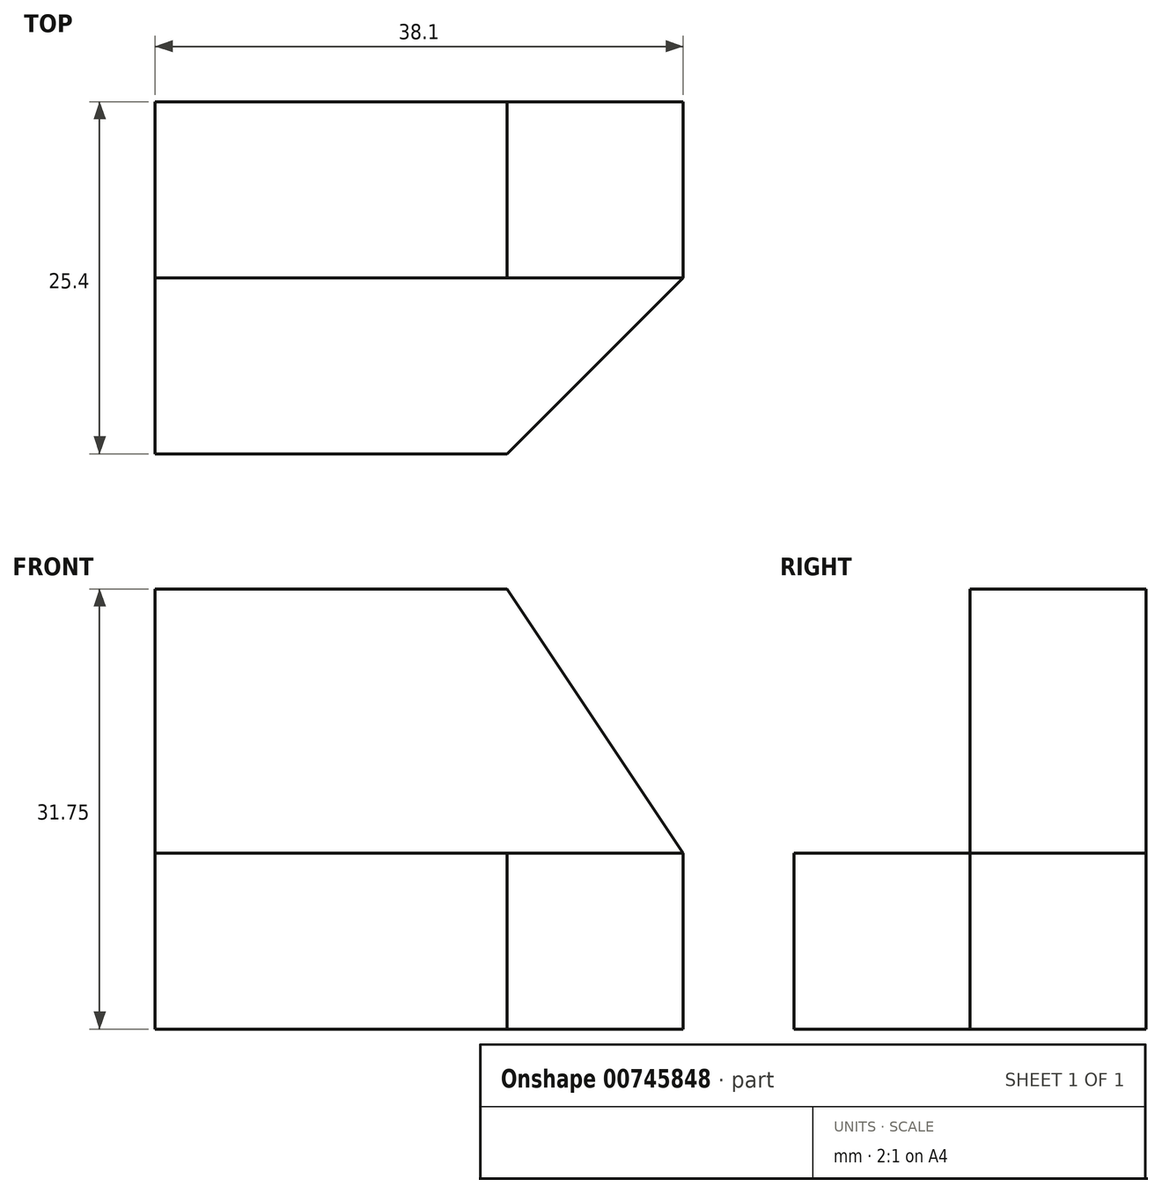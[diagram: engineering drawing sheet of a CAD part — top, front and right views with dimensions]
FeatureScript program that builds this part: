
annotation { "Feature Type Name" : "Feature", "Feature Type Description" : "" }
export const myFeature = defineFeature(function(context is Context, id is Id, definition is map)
    precondition{}
    {
        {
            var Q0;
            Q0=qCreatedBy(makeId("Front.planeOp"),FACE);
            var sketch = newSketch(context, id + "F0", { "sketchPlane" : qUnion([Q0])});
            skLineSegment(sketch, "E0", {"start": v(0, 0) * mm, "end": v(0, 31.75) * mm});
            skLineSegment(sketch, "E1", {"start": v(0, 31.75) * mm, "end": v(38.1, 31.75) * mm});
            skLineSegment(sketch, "E2", {"start": v(38.1, 31.75) * mm, "end": v(38.1, 0) * mm});
            skLineSegment(sketch, "E3", {"start": v(38.1, 0) * mm, "end": v(0, 0) * mm});
            skSolve(sketch);
        }
        {
            var Q0;
            Q0 = qSketchRegion(id + "F0", true);
            extrude(context, id + "F1", {"entities" : qUnion([Q0]), "depth" : 25.4 * mm, "offsetDistance" : 25.4 * mm});
        }
        {
            var Q0;
            Q0=makeQuery(id+"F1.opExtrude","SWEPT_FACE",FACE,{"disambiguationData":[OSD([sQuery(id+"F0.wireOp",EDGE,"E1")])]});
            var sketch = newSketch(context, id + "F2", { "sketchPlane" : qUnion([Q0])});
            skLineSegment(sketch, "E4", {"start": v(0, -12.7) * mm, "end": v(38.1, -12.7) * mm});
            skSolve(sketch);
        }
        {
            var Q0;
            {var subQ0=sQuery(id+"F2.wireOp",EDGE,"E4");Q0=makeQuery(id+"F2.imprint","IMPRINT",FACE,{"disambiguationData":[TD([[makeQuery(id+"F2.imprint","IMPRINT",EDGE,{"derivedFrom":subQ0}),-1.0]])]});}
            extrude(context, id + "F3", {"entities" : qUnion([Q0]), "operationType" : NewBodyOperationType.REMOVE, "oppositeDirection" : true, "depth" : 19.05 * mm, "offsetDistance" : 25.4 * mm});
        }
        {
            var Q0;
            Q0=makeQuery(id+"F3.boolean.opBoolean","COPY",FACE,{"derivedFrom":makeQuery(id+"F3.opExtrude","CAP_FACE",FACE,{"disambiguationData":[OSD([sQuery(id+"F0.wireOp",EDGE,"E0"),sQuery(id+"F0.wireOp",EDGE,"E1"),sQuery(id+"F0.wireOp",EDGE,"E2"),sQuery(id+"F2.wireOp",EDGE,"E4")])],"isStart":false})});
            var sketch = newSketch(context, id + "F4", { "sketchPlane" : qUnion([Q0])});
            skLineSegment(sketch, "E5", {"start": v(38.1, -12.7) * mm, "end": v(25.4, -25.4) * mm});
            skSolve(sketch);
        }
        {
            var Q0;
            {var subQ0=sQuery(id+"F4.wireOp",EDGE,"E5");Q0=makeQuery(id+"F4.imprint","IMPRINT",FACE,{"disambiguationData":[TD([[makeQuery(id+"F4.imprint","IMPRINT",EDGE,{"derivedFrom":subQ0}),1.0]])]});}
            extrude(context, id + "F5", {"entities" : qUnion([Q0]), "operationType" : NewBodyOperationType.REMOVE, "endBound" : BoundingType.THROUGH_ALL, "oppositeDirection" : true, "depth" : 25.4 * mm, "offsetDistance" : 25.4 * mm});
        }
        {
            var Q0;
            Q0=makeQuery(id+"F3.boolean.opBoolean","COPY",FACE,{"derivedFrom":makeQuery(id+"F3.opExtrude","SWEPT_FACE",FACE,{"disambiguationData":[OSD([sQuery(id+"F2.wireOp",EDGE,"E4")])]})});
            var sketch = newSketch(context, id + "F6", { "sketchPlane" : qUnion([Q0])});
            skLineSegment(sketch, "E6", {"start": v(38.1, 12.7) * mm, "end": v(25.4, 31.75) * mm});
            skSolve(sketch);
        }
        {
            var Q0;
            {var subQ0=sQuery(id+"F6.wireOp",EDGE,"E6");Q0=makeQuery(id+"F6.imprint","IMPRINT",FACE,{"disambiguationData":[TD([[makeQuery(id+"F6.imprint","IMPRINT",EDGE,{"derivedFrom":subQ0}),-1.0]])]});}
            extrude(context, id + "F7", {"entities" : qUnion([Q0]), "operationType" : NewBodyOperationType.REMOVE, "endBound" : BoundingType.THROUGH_ALL, "oppositeDirection" : true, "depth" : 25.4 * mm, "offsetDistance" : 25.4 * mm});
        }
    });
